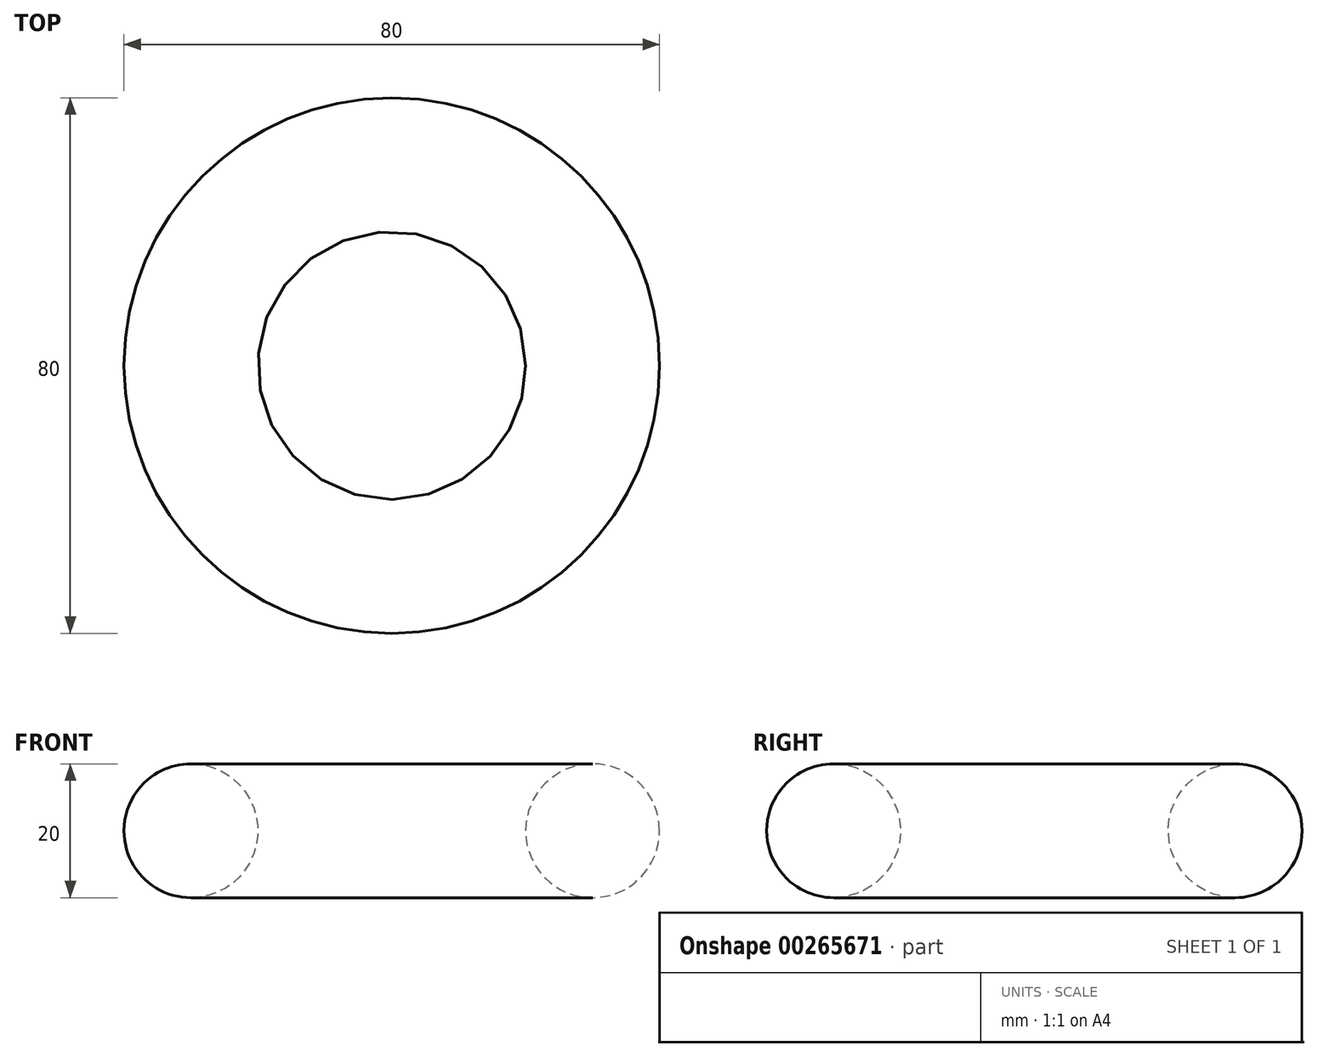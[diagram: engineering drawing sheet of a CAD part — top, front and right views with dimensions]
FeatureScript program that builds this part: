
annotation { "Feature Type Name" : "Feature", "Feature Type Description" : "" }
export const myFeature = defineFeature(function(context is Context, id is Id, definition is map)
    precondition{}
    {
        {
            var Q0;
            Q0=qCreatedBy(makeId("Front.planeOp"),FACE);
            var sketch = newSketch(context, id + "F0", { "sketchPlane" : qUnion([Q0])});
            skCircle(sketch, "E0", {"center": v(30, 0) * mm, "radius": 10 * mm});
            skLineSegment(sketch, "E1", {"start": v(0, 55.43) * mm, "end": v(0, -49.12) * mm, "construction": true});
            skSolve(sketch);
        }
        {
            var Q0;
            Q0=makeQuery(id+"F0.imprint","IMPRINT",FACE,{"disambiguationData":[TD([[makeQuery(id+"F0.imprint","IMPRINT",EDGE,{"derivedFrom":sQuery(id+"F0.wireOp",EDGE,"E0")}),1.0]])]});
            var Q1;
            Q1=sQuery(id+"F0.wireOp",EDGE,"E1");
            revolve(context, id + "F1", {"entities" : qUnion([Q0]), "axis" : qUnion([Q1]), "revolveType" : RevolveType.FULL});
        }
    });
